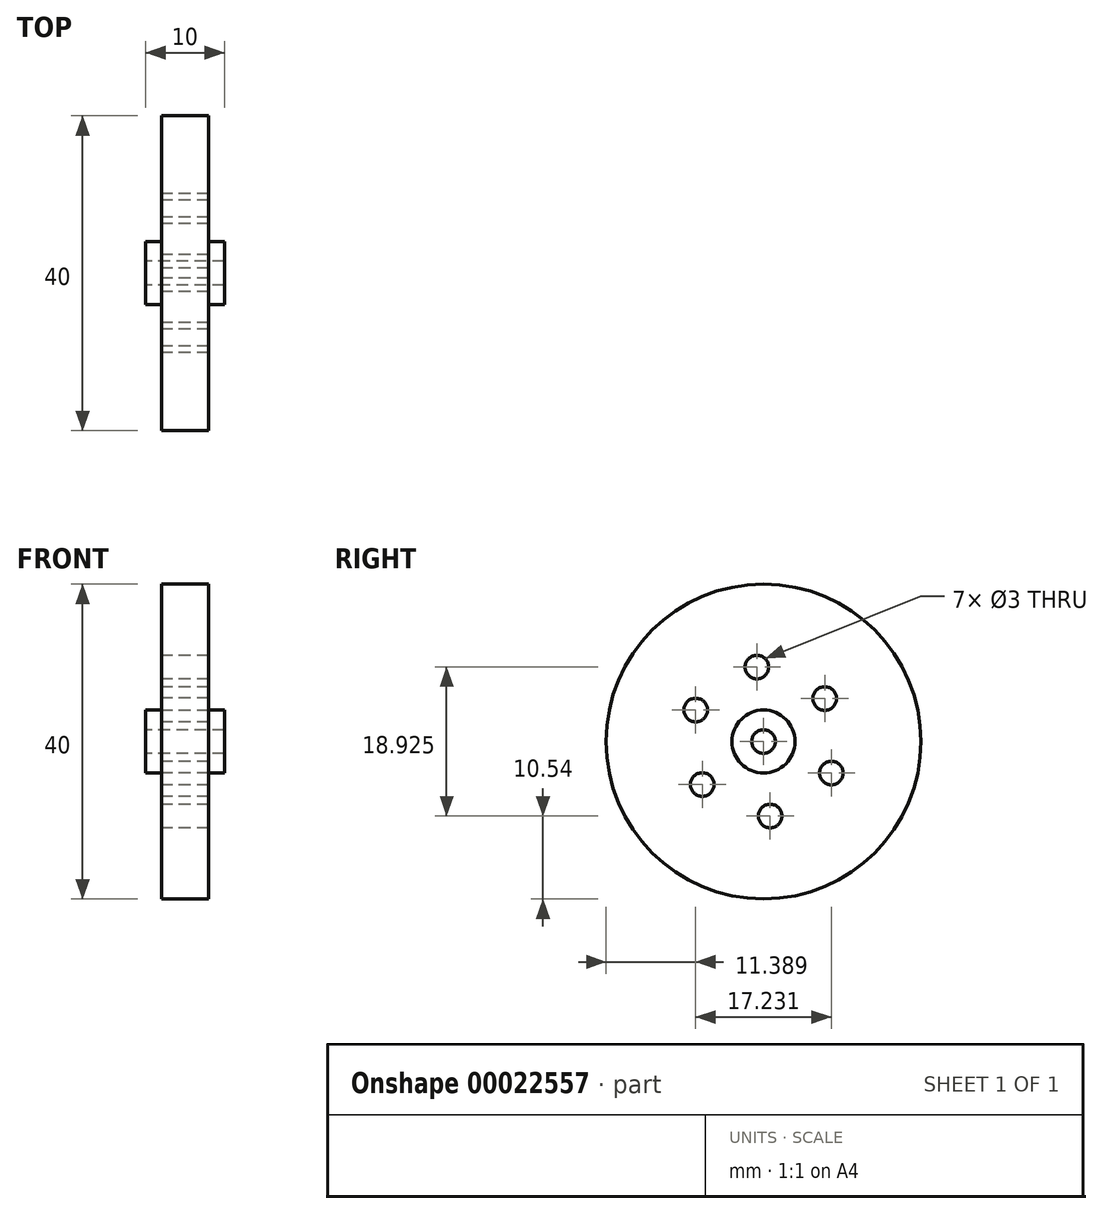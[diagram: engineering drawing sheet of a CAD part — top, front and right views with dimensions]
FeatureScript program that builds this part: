
annotation { "Feature Type Name" : "Feature", "Feature Type Description" : "" }
export const myFeature = defineFeature(function(context is Context, id is Id, definition is map)
    precondition{}
    {
        {
            var Q0;
            Q0=qCreatedBy(makeId("Right.planeOp"),FACE);
            var sketch = newSketch(context, id + "F0", { "sketchPlane" : qUnion([Q0])});
            skCircle(sketch, "E0", {"center": v(-31.6, 23.8) * mm, "radius": 20 * mm});
            skCircle(sketch, "E1", {"center": v(-31.6, 23.8) * mm, "radius": 4 * mm});
            skCircle(sketch, "E2", {"center": v(-31.6, 23.8) * mm, "radius": 1.5 * mm});
            skCircle(sketch, "E3", {"center": v(-32.44, 33.26) * mm, "radius": 1.5 * mm});
            skCircle(sketch, "E4.1.0", {"center": v(-40.21, 27.8) * mm, "radius": 1.5 * mm});
            skCircle(sketch, "E4.2.0", {"center": v(-39.37, 18.33) * mm, "radius": 1.5 * mm});
            skCircle(sketch, "E4.3.0", {"center": v(-30.75, 14.33) * mm, "radius": 1.5 * mm});
            skCircle(sketch, "E4.4.0", {"center": v(-22.98, 19.79) * mm, "radius": 1.5 * mm});
            skCircle(sketch, "E4.5.0", {"center": v(-23.82, 29.25) * mm, "radius": 1.5 * mm});
            skSolve(sketch);
        }
        {
            var Q0;
            Q0=makeQuery(id+"F0.imprint","IMPRINT",FACE,{"disambiguationData":[TD([[makeQuery(id+"F0.imprint","IMPRINT",EDGE,{"derivedFrom":sQuery(id+"F0.wireOp",EDGE,"E0")}),1.0]])]});
            var Q1;
            Q1=makeQuery(id+"F0.imprint","IMPRINT",FACE,{"disambiguationData":[TD([[makeQuery(id+"F0.imprint","IMPRINT",EDGE,{"derivedFrom":sQuery(id+"F0.wireOp",EDGE,"E1")}),1.0]])]});
            extrude(context, id + "F1", {"entities" : qUnion([Q0, Q1]), "depth" : 6 * mm});
        }
        {
            var Q0;
            Q0=makeQuery(id+"F0.imprint","IMPRINT",FACE,{"disambiguationData":[TD([[makeQuery(id+"F0.imprint","IMPRINT",EDGE,{"derivedFrom":sQuery(id+"F0.wireOp",EDGE,"E1")}),1.0]])]});
            extrude(context, id + "F2", {"entities" : qUnion([Q0]), "operationType" : NewBodyOperationType.ADD, "depth" : 8 * mm});
        }
        {
            var Q0;
            Q0=makeQuery(id+"F0.imprint","IMPRINT",FACE,{"disambiguationData":[TD([[makeQuery(id+"F0.imprint","IMPRINT",EDGE,{"derivedFrom":sQuery(id+"F0.wireOp",EDGE,"E1")}),1.0]])]});
            extrude(context, id + "F3", {"entities" : qUnion([Q0]), "operationType" : NewBodyOperationType.ADD, "oppositeDirection" : true, "depth" : 2 * mm});
        }
    });
